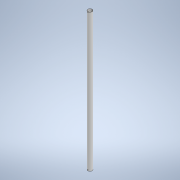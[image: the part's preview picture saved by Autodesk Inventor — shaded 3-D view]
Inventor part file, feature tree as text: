
AUTODESK INVENTOR PART (.ipt)
format: ipt  version: 2022 (Build 260153000, 153)  size: 117,248 bytes
history: native  units: mm
features: extrude x2, sketch x2
ambient origin geometry x8: Origin, YZ Plane, XZ Plane, XY Plane, X Axis, Y Axis, Z Axis, Center Point
bodies: Solid1 (feature_tree)
feature tree (4):
  extrude  "Extrusion1"  Depth=31.0mm
  extrude  "Extrusion2"  Depth=6.0mm
  sketch  "Sketch1"  dims[d0=30.0mm d1=31.0mm]
  sketch  "Sketch2"  dims[d2=1000.0mm d3=0.0mm d4=6.0mm d5=90.0deg d6=3.0mm d7=6.0mm d8=3.0mm d9=40.0mm d10=0.0mm]
